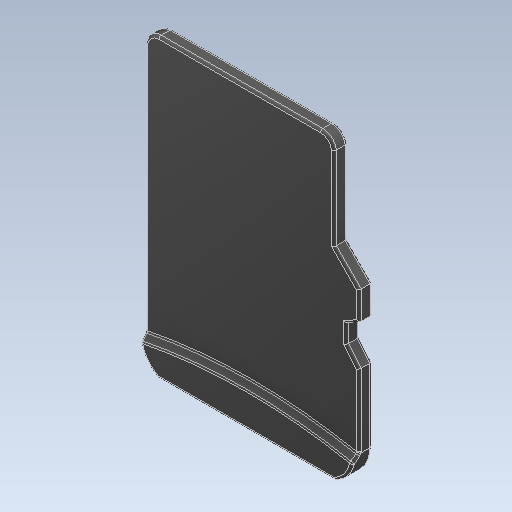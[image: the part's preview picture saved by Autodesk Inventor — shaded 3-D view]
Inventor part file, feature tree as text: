
AUTODESK INVENTOR PART (.ipt)
format: ipt  version: 2021 (Build 250183000, 183)  size: 184,320 bytes
history: native  units: mm
features: fillet x1
ambient origin geometry x8: Origin, YZ Plane, XZ Plane, XY Plane, X Axis, Y Axis, Z Axis, Center Point
bodies: Solid1 (feature_tree)
feature tree (1):
  fillet  "Fillet2"  [1 undecoded]
note: 1 required parameter value undecoded (feature->parameter linkage not recoverable at this tier; creation-order binding heuristic only, values carry confidence <= 0.55)
